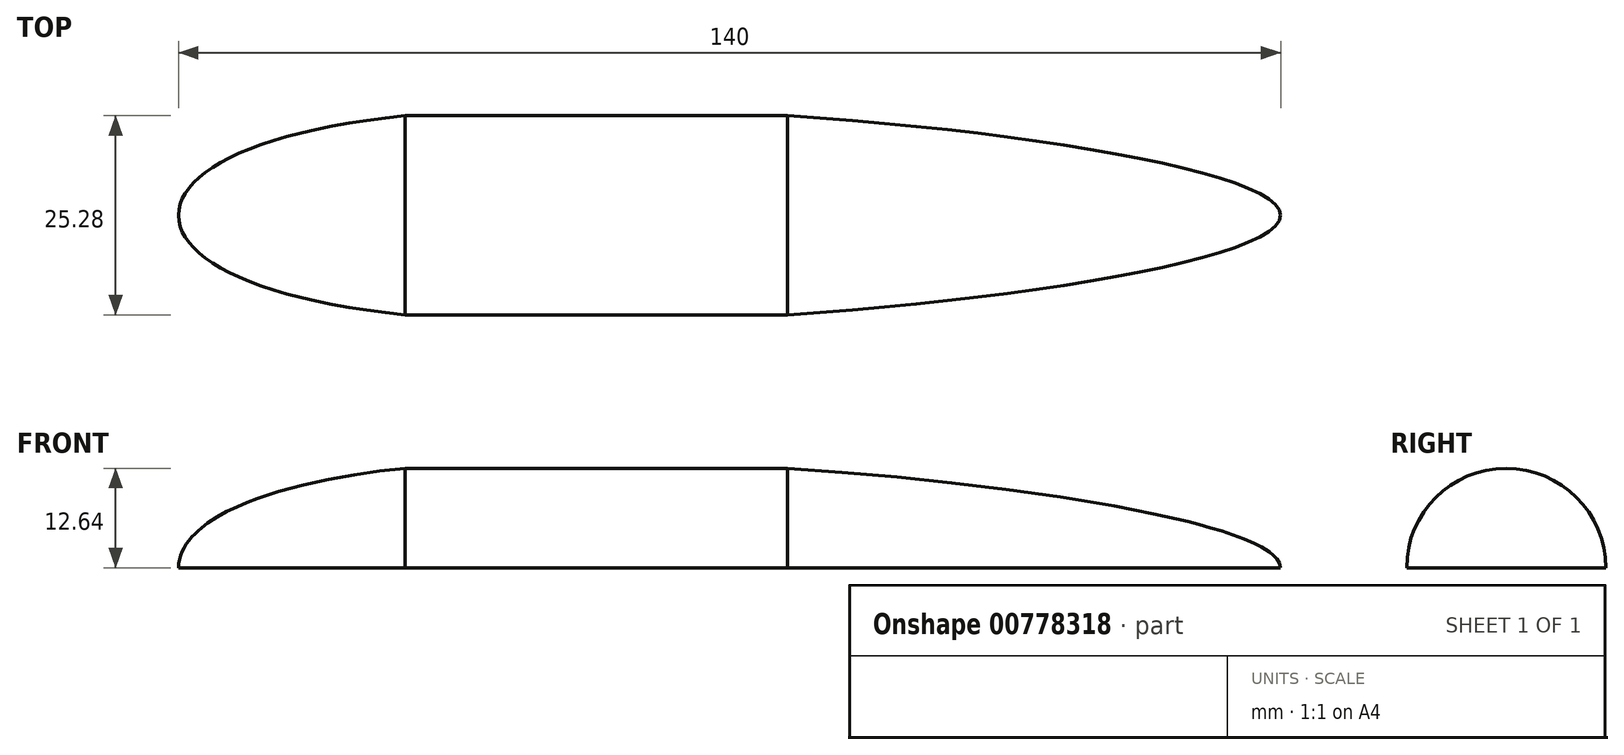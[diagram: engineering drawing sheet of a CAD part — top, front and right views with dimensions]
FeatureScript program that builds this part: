
annotation { "Feature Type Name" : "Feature", "Feature Type Description" : "" }
export const myFeature = defineFeature(function(context is Context, id is Id, definition is map)
    precondition{}
    {
        {
            var Q0;
            Q0=qCreatedBy(makeId("Top.planeOp"),FACE);
            var sketch = newSketch(context, id + "F0", { "sketchPlane" : qUnion([Q0])});
            skLineSegment(sketch, "E0.bottom", {"start": v(-75.15, 0) * mm, "end": v(64.85, 0) * mm});
            skLineSegment(sketch, "E0.top", {"start": v(-75.15, 25.28) * mm, "end": v(64.85, 25.28) * mm});
            skLineSegment(sketch, "E0.left", {"start": v(-75.15, 0) * mm, "end": v(-75.15, 25.28) * mm});
            skLineSegment(sketch, "E0.right", {"start": v(64.85, 0) * mm, "end": v(64.85, 25.28) * mm});
            skFitSpline(sketch, "E1", {"points": [v(-75.15, 12.64) * mm, v(-46.38, 25.28) * mm, v(64.85, 12.64) * mm, v(-46.1, 0) * mm, v(-75.15, 12.64) * mm]});
            skLineSegment(sketch, "E2", {"start": v(-75.15, 12.64) * mm, "end": v(64.85, 12.64) * mm});
            skSolve(sketch);
        }
        {
            var Q0;
            {var subQ0=sQuery(id+"F0.wireOp",EDGE,"E2");Q0=makeQuery(id+"F0.imprint","IMPRINT",FACE,{"disambiguationData":[TD([[makeQuery(id+"F0.imprint","IMPRINT",EDGE,{"derivedFrom":subQ0}),1.0]])]});}
            var Q1;
            Q1=sQuery(id+"F0.wireOp",EDGE,"E2");
            revolve(context, id + "F1", {"surfaceOperationType" : NewSurfaceOperationType.NEW, "entities" : qUnion([Q0]), "axis" : qUnion([Q1]), "revolveType" : RevolveType.ONE_DIRECTION, "angle" : 180 * degree});
        }
    });
